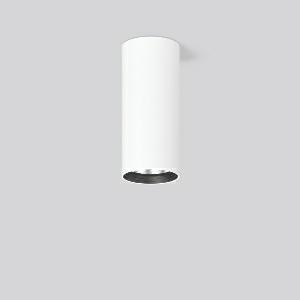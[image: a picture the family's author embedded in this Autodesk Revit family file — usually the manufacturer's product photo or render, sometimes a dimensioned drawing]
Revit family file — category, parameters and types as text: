
# Revit family: heledon_mini_a_931209_002_2_4473
name_source: partatom
category: Lighting Fixtures
units: mm (PartAtom-declared; Revit-internal decimal feet)

## family parameters
Cut with Voids When Loaded = No
Host = Face
Light Source = No
Part Type = Normal
Room Calculation Point = No
Round Connector Dimension = Use Diameter
Shared = No

## types (1)
- HELEDON mini A (1 x LED Modul 927, 3300 lm, 2700)
    Apparent Load = 29 VA
    Approval mark = CE
    CIE Flux Codes = 99 100 100 100 100
    Color Rendering = 92
    Color Temperature = 2700
    Default Elevation = 1800 mm
    Description = Series: HELEDON mini
Cylindrical surface-mounted downlight. Housing: die-cast aluminium, powder-coated. Internal ceiling frame polycarbonate with bayonet mounting. Black plastic ring and recessed LED to prevent glare from the side. Optical assembly with reflector made of MIRO-Silver with 98% total light reflection for outstanding efficiency - can be changed without tools. Best colour rendering index Ra>90. Suitable for Ceiling mounting. Easy installation with a separate ceiling frame with bayonet mounting and plug connection. Driver integrated. Connected via plug-in connector. High quality converter without flickering and stroboscopic effect. The following accessories can be mounted without use of tools: interchangeable lenses, decorative glasses, honeycomb louvre, clear and frosted diffusers, white interchangeable plastic ring. 
Colour: traffic white, matt (RAL 9016)
Diameter: 87 mm
Height: 197 mm
Lamp: LED
Socket: without socket
Colour temperature: 2700K
Colour rendering index (CRI): 92
System power: 29 W
Rated luminous flux: 3300 lm
Luminous efficiency: 114 lm/W
Control gear: Regulated power supply
Protection class: I
Type of protection: IP 20
    Height = 197 mm
    Lamp = 1 x LED Modul 927
    Lamp Light Flux = 3300 lm
    Lamp count = 1
    Length = 87 mm
    Lifetime = 50000 h
    Luminous efficacy = 114 lm/W
    Manufacturer = RZB
    ModVariant = No
    Model = 931209.002.2
    Mounting Place = Ceiling
    Mounting Type = Surface mounted
    Number of Poles = 1
    OnlyDefault = Yes
    Power Factor = 1
    Product Name = HELEDON mini A
    Product group = Surface mounted downlights
    ProductGroupID = 302
    Protection Class = Protection class I
    Protection Degree = IP 20
    RLX_Detail_Level = 1
    RLX_Emergency_Light_Flux = 0 lm
    RLX_Emergency_Type = 0
    RLX_Emergency_Type_DB = No
    RlxData = <blob elided: 107477 chars, md5=175a1f2a>
    Socket = socket
    Standby Power = 0 W
    System Light Flux = 3300 lm
    System Power = 29 W
    Type Comments = Product without accessories
    Type Image = 931188.002.jpg
    URL = http://relux.com
    VarID = ---
    Voltage = 230 V
    Voltage Range = 220-240 V
    Weight = 0.00 kg
    Width = 0 mm  [stored 0 ft]

note: [stored X ft] marks values corroborated as IEEE doubles in the binary element streams (Revit-internal decimal feet)

## geometry (parser evidence)
native form markers: Blend x4, Sweep x9
no freeform markers — native parametric forms only
